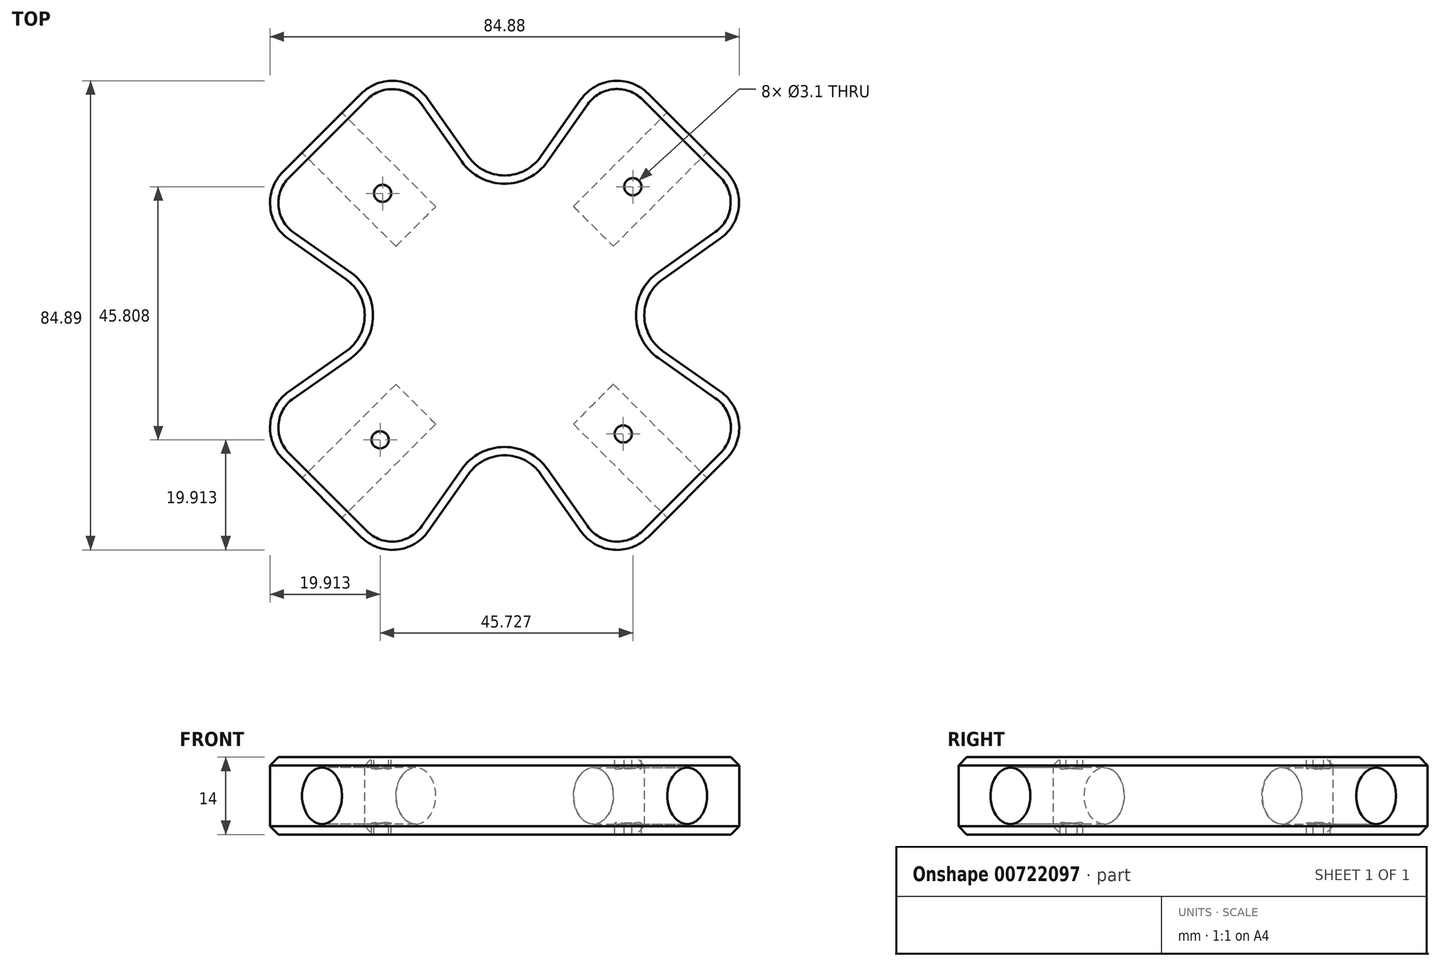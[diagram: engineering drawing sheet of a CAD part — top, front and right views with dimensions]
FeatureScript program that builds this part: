
annotation { "Feature Type Name" : "Feature", "Feature Type Description" : "" }
export const myFeature = defineFeature(function(context is Context, id is Id, definition is map)
    precondition{}
    {
        {
            var Q0;
            Q0=qCreatedBy(makeId("Top.planeOp"),FACE);
            var sketch = newSketch(context, id + "F0", { "sketchPlane" : qUnion([Q0])});
            skLineSegment(sketch, "E0", {"start": v(0, 0) * mm, "end": v(38.75, 38.75) * mm});
            skLineSegment(sketch, "E1", {"start": v(0, 0) * mm, "end": v(38.75, -38.75) * mm});
            skLineSegment(sketch, "E2", {"start": v(0, 0) * mm, "end": v(-38.75, -38.75) * mm});
            skLineSegment(sketch, "E3", {"start": v(0, 0) * mm, "end": v(-38.75, 38.75) * mm});
            skCircle(sketch, "E4.cCircle", {"center": v(0, 0) * mm, "radius": 54.8 * mm, "construction": true});
            skLineSegment(sketch, "E4.0", {"start": v(0, 54.8) * mm, "end": v(38.75, 38.75) * mm});
            skLineSegment(sketch, "E4.1", {"start": v(38.75, 38.75) * mm, "end": v(46.78, 19.38) * mm});
            skLineSegment(sketch, "E4.2", {"start": v(54.8, 0) * mm, "end": v(46.84, -19.24) * mm});
            skLineSegment(sketch, "E4.3", {"start": v(38.75, -38.75) * mm, "end": v(19.24, -46.84) * mm});
            skLineSegment(sketch, "E4.4", {"start": v(0, -54.8) * mm, "end": v(-19.24, -46.84) * mm});
            skLineSegment(sketch, "E4.5", {"start": v(-38.75, -38.75) * mm, "end": v(-46.84, -19.24) * mm});
            skLineSegment(sketch, "E4.6", {"start": v(-54.8, 0) * mm, "end": v(-38.75, 38.75) * mm});
            skLineSegment(sketch, "E4.7", {"start": v(-38.75, 38.75) * mm, "end": v(0, 54.8) * mm});
            skCircle(sketch, "E5.cCircle", {"center": v(-54.8, 0) * mm, "radius": 22.22 * mm, "construction": true});
            skLineSegment(sketch, "E5.0", {"start": v(-32.58, 0) * mm, "end": v(-43.7, -19.24) * mm});
            skLineSegment(sketch, "E5.1", {"start": v(-43.7, -19.24) * mm, "end": v(-65.92, -19.24) * mm});
            skLineSegment(sketch, "E5.2", {"start": v(-65.92, -19.24) * mm, "end": v(-77.03, 0) * mm});
            skLineSegment(sketch, "E5.3", {"start": v(-77.03, 0) * mm, "end": v(-65.92, 19.24) * mm});
            skLineSegment(sketch, "E5.4", {"start": v(-65.92, 19.24) * mm, "end": v(-46.84, 19.24) * mm});
            skLineSegment(sketch, "E5.5", {"start": v(-43.7, 19.24) * mm, "end": v(-32.58, 0) * mm});
            skCircle(sketch, "E6.cCircle", {"center": v(0, -54.8) * mm, "radius": 22.22 * mm, "construction": true});
            skLineSegment(sketch, "E6.0", {"start": v(0, -32.58) * mm, "end": v(19.24, -43.7) * mm});
            skLineSegment(sketch, "E6.1", {"start": v(19.24, -43.7) * mm, "end": v(19.24, -65.92) * mm});
            skLineSegment(sketch, "E6.2", {"start": v(19.24, -65.92) * mm, "end": v(0, -77.03) * mm});
            skLineSegment(sketch, "E6.3", {"start": v(0, -77.03) * mm, "end": v(-19.24, -65.92) * mm});
            skLineSegment(sketch, "E6.4", {"start": v(-19.24, -65.92) * mm, "end": v(-19.24, -43.7) * mm});
            skLineSegment(sketch, "E6.5", {"start": v(-19.24, -43.7) * mm, "end": v(0, -32.58) * mm});
            skCircle(sketch, "E7.cCircle", {"center": v(54.8, 0) * mm, "radius": 22.22 * mm, "construction": true});
            skLineSegment(sketch, "E7.0", {"start": v(32.58, 0) * mm, "end": v(43.7, 19.24) * mm});
            skLineSegment(sketch, "E7.1", {"start": v(43.7, 19.24) * mm, "end": v(65.92, 19.24) * mm});
            skLineSegment(sketch, "E7.2", {"start": v(65.92, 19.24) * mm, "end": v(77.03, 0) * mm});
            skLineSegment(sketch, "E7.3", {"start": v(77.03, 0) * mm, "end": v(65.92, -19.24) * mm});
            skLineSegment(sketch, "E7.4", {"start": v(65.92, -19.24) * mm, "end": v(43.7, -19.24) * mm});
            skLineSegment(sketch, "E7.5", {"start": v(43.7, -19.24) * mm, "end": v(32.58, 0) * mm});
            skCircle(sketch, "E8.cCircle", {"center": v(0, 54.8) * mm, "radius": 22.22 * mm, "construction": true});
            skLineSegment(sketch, "E8.0", {"start": v(0, 32.58) * mm, "end": v(-19.24, 43.7) * mm});
            skLineSegment(sketch, "E8.1", {"start": v(-19.24, 43.7) * mm, "end": v(-19.24, 46.84) * mm});
            skLineSegment(sketch, "E8.2", {"start": v(-19.24, 65.92) * mm, "end": v(0, 77.03) * mm});
            skLineSegment(sketch, "E8.3", {"start": v(0, 77.03) * mm, "end": v(19.24, 65.92) * mm});
            skLineSegment(sketch, "E8.4", {"start": v(19.24, 65.92) * mm, "end": v(19.24, 46.84) * mm});
            skLineSegment(sketch, "E8.5", {"start": v(19.24, 43.7) * mm, "end": v(0, 32.58) * mm});
            skLineSegment(sketch, "E9", {"start": v(-46.84, 19.24) * mm, "end": v(-43.7, 19.24) * mm});
            skLineSegment(sketch, "E10", {"start": v(-46.84, -19.24) * mm, "end": v(-54.8, 0) * mm});
            skLineSegment(sketch, "E11", {"start": v(-19.24, 46.84) * mm, "end": v(-19.24, 65.92) * mm});
            skLineSegment(sketch, "E12", {"start": v(19.24, 46.84) * mm, "end": v(19.24, 43.7) * mm});
            skLineSegment(sketch, "E13", {"start": v(46.78, 19.38) * mm, "end": v(54.8, 0) * mm});
            skLineSegment(sketch, "E14", {"start": v(46.84, -19.24) * mm, "end": v(38.75, -38.75) * mm});
            skLineSegment(sketch, "E15", {"start": v(19.24, -46.84) * mm, "end": v(0, -54.8) * mm});
            skLineSegment(sketch, "E16", {"start": v(-19.24, -46.84) * mm, "end": v(-38.75, -38.75) * mm});
            skLineSegment(sketch, "E17", {"start": v(-46.84, 19.24) * mm, "end": v(-19.24, 46.84) * mm});
            skLineSegment(sketch, "E18", {"start": v(19.24, 46.84) * mm, "end": v(46.78, 19.38) * mm});
            skLineSegment(sketch, "E19", {"start": v(46.84, -19.24) * mm, "end": v(19.24, -46.84) * mm});
            skLineSegment(sketch, "E20", {"start": v(-46.84, -19.24) * mm, "end": v(-19.24, -46.84) * mm});
            skLineSegment(sketch, "E21.bottom", {"start": v(19.38, -19.38) * mm, "end": v(-19.38, -19.38) * mm});
            skLineSegment(sketch, "E21.top", {"start": v(19.38, 19.38) * mm, "end": v(-19.38, 19.38) * mm});
            skLineSegment(sketch, "E21.left", {"start": v(19.38, -19.38) * mm, "end": v(19.38, 19.38) * mm});
            skLineSegment(sketch, "E21.right", {"start": v(-19.38, -19.38) * mm, "end": v(-19.38, 19.38) * mm});
            skLineSegment(sketch, "E22", {"start": v(-46.84, 19.24) * mm, "end": v(-19.38, 0) * mm});
            skLineSegment(sketch, "E23", {"start": v(-19.38, 0) * mm, "end": v(-46.84, -19.24) * mm});
            skLineSegment(sketch, "E24", {"start": v(-19.24, -46.84) * mm, "end": v(0, -19.38) * mm});
            skLineSegment(sketch, "E25", {"start": v(19.24, -46.84) * mm, "end": v(0, -19.38) * mm});
            skLineSegment(sketch, "E26", {"start": v(46.84, -19.24) * mm, "end": v(19.38, 0) * mm});
            skLineSegment(sketch, "E27", {"start": v(46.78, 19.38) * mm, "end": v(19.38, 0) * mm});
            skLineSegment(sketch, "E28", {"start": v(19.24, 46.84) * mm, "end": v(0, 19.38) * mm});
            skLineSegment(sketch, "E29", {"start": v(0, 19.38) * mm, "end": v(-19.24, 46.84) * mm});
            skSolve(sketch);
        }
        {
            var Q0;
            {var subQ0=sQuery(id+"F0.wireOp",EDGE,"E9");Q0=makeQuery(id+"F0.imprint","IMPRINT",FACE,{"disambiguationData":[TD([[makeQuery(id+"F0.imprint","IMPRINT",EDGE,{"derivedFrom":subQ0}),1.0]])]});}
            var Q1;
            {var subQ1=sQuery(id+"F0.wireOp",EDGE,"E2");var subQ3=sQuery(id+"F0.wireOp",EDGE,"E21.right");var subQ4=makeQuery(id+"F0.imprint","INTERSECT",VERTEX,{"derivedFrom":[subQ1,sQuery(id+"F0.wireOp",EDGE,"E21.bottom"),subQ3]});Q1=makeQuery(id+"F0.imprint","IMPRINT",FACE,{"disambiguationData":[TD([[makeQuery(id+"F0.imprint","IMPRINT",EDGE,{"disambiguationData":[TD([[subQ4,-1.0]])],"derivedFrom":subQ3}),-1.0]])]});}
            var Q2;
            {var subQ2=sQuery(id+"F0.wireOp",EDGE,"E5.1");var subQ6=sQuery(id+"F0.wireOp",EDGE,"E5.0");var subQ7=makeQuery(id+"F0.imprint","INTERSECT",VERTEX,{"derivedFrom":[subQ6,subQ2]});Q2=makeQuery(id+"F0.imprint","IMPRINT",FACE,{"disambiguationData":[TD([[makeQuery(id+"F0.imprint","IMPRINT",EDGE,{"disambiguationData":[TD([[subQ7,1.0]])],"derivedFrom":subQ6}),1.0]])]});}
            var Q3;
            {var subQ0=sQuery(id+"F0.wireOp",EDGE,"E6.5");var subQ1=sQuery(id+"F0.wireOp",EDGE,"E6.4");var subQ2=makeQuery(id+"F0.imprint","INTERSECT",VERTEX,{"derivedFrom":[subQ1,subQ0]});Q3=makeQuery(id+"F0.imprint","IMPRINT",FACE,{"disambiguationData":[TD([[makeQuery(id+"F0.imprint","IMPRINT",EDGE,{"disambiguationData":[TD([[subQ2,-1.0]])],"derivedFrom":subQ0}),1.0]])]});}
            var Q4;
            {var subQ2=sQuery(id+"F0.wireOp",EDGE,"E6.1");var subQ6=sQuery(id+"F0.wireOp",EDGE,"E6.0");var subQ7=makeQuery(id+"F0.imprint","INTERSECT",VERTEX,{"derivedFrom":[subQ6,subQ2]});Q4=makeQuery(id+"F0.imprint","IMPRINT",FACE,{"disambiguationData":[TD([[makeQuery(id+"F0.imprint","IMPRINT",EDGE,{"disambiguationData":[TD([[subQ7,1.0]])],"derivedFrom":subQ6}),1.0]])]});}
            var Q5;
            {var subQ0=sQuery(id+"F0.wireOp",EDGE,"E1");var subQ3=sQuery(id+"F0.wireOp",EDGE,"E21.left");var subQ5=makeQuery(id+"F0.imprint","INTERSECT",VERTEX,{"derivedFrom":[subQ0,sQuery(id+"F0.wireOp",EDGE,"E21.bottom"),subQ3]});Q5=makeQuery(id+"F0.imprint","IMPRINT",FACE,{"disambiguationData":[TD([[makeQuery(id+"F0.imprint","IMPRINT",EDGE,{"disambiguationData":[TD([[subQ5,-1.0]])],"derivedFrom":subQ3}),1.0]])]});}
            var Q6;
            {var subQ1=sQuery(id+"F0.wireOp",EDGE,"E1");var subQ3=sQuery(id+"F0.wireOp",EDGE,"E21.bottom");var subQ4=makeQuery(id+"F0.imprint","INTERSECT",VERTEX,{"derivedFrom":[subQ1,subQ3,sQuery(id+"F0.wireOp",EDGE,"E21.left")]});Q6=makeQuery(id+"F0.imprint","IMPRINT",FACE,{"disambiguationData":[TD([[makeQuery(id+"F0.imprint","IMPRINT",EDGE,{"disambiguationData":[TD([[subQ4,-1.0]])],"derivedFrom":subQ3}),-1.0]])]});}
            var Q7;
            {var subQ1=sQuery(id+"F0.wireOp",EDGE,"E0");var subQ3=sQuery(id+"F0.wireOp",EDGE,"E21.top");var subQ4=makeQuery(id+"F0.imprint","INTERSECT",VERTEX,{"derivedFrom":[subQ1,subQ3,sQuery(id+"F0.wireOp",EDGE,"E21.left")]});Q7=makeQuery(id+"F0.imprint","IMPRINT",FACE,{"disambiguationData":[TD([[makeQuery(id+"F0.imprint","IMPRINT",EDGE,{"disambiguationData":[TD([[subQ4,-1.0]])],"derivedFrom":subQ3}),1.0]])]});}
            var Q8;
            {var subQ0=sQuery(id+"F0.wireOp",EDGE,"E7.1");var subQ1=sQuery(id+"F0.wireOp",EDGE,"E7.0");var subQ2=makeQuery(id+"F0.imprint","INTERSECT",VERTEX,{"derivedFrom":[subQ1,subQ0]});Q8=makeQuery(id+"F0.imprint","IMPRINT",FACE,{"disambiguationData":[TD([[makeQuery(id+"F0.imprint","IMPRINT",EDGE,{"disambiguationData":[TD([[subQ2,1.0]])],"derivedFrom":subQ1}),1.0]])]});}
            var Q9;
            {var subQ2=sQuery(id+"F0.wireOp",EDGE,"E12");Q9=makeQuery(id+"F0.imprint","IMPRINT",FACE,{"disambiguationData":[TD([[makeQuery(id+"F0.imprint","IMPRINT",EDGE,{"derivedFrom":subQ2}),1.0]])]});}
            var Q10;
            {var subQ2=sQuery(id+"F0.wireOp",EDGE,"E8.1");Q10=makeQuery(id+"F0.imprint","IMPRINT",FACE,{"disambiguationData":[TD([[makeQuery(id+"F0.imprint","IMPRINT",EDGE,{"derivedFrom":subQ2}),1.0]])]});}
            var Q11;
            {var subQ0=sQuery(id+"F0.wireOp",EDGE,"E7.5");var subQ1=sQuery(id+"F0.wireOp",EDGE,"E7.4");var subQ2=makeQuery(id+"F0.imprint","INTERSECT",VERTEX,{"derivedFrom":[subQ1,subQ0]});Q11=makeQuery(id+"F0.imprint","IMPRINT",FACE,{"disambiguationData":[TD([[makeQuery(id+"F0.imprint","IMPRINT",EDGE,{"disambiguationData":[TD([[subQ2,-1.0]])],"derivedFrom":subQ0}),1.0]])]});}
            var Q12;
            {var subQ0=sQuery(id+"F0.wireOp",EDGE,"E9");Q12=makeQuery(id+"F0.imprint","IMPRINT",FACE,{"disambiguationData":[TD([[makeQuery(id+"F0.imprint","IMPRINT",EDGE,{"derivedFrom":subQ0}),-1.0]])]});}
            var Q13;
            {var subQ0=sQuery(id+"F0.wireOp",EDGE,"E8.1");Q13=makeQuery(id+"F0.imprint","IMPRINT",FACE,{"disambiguationData":[TD([[makeQuery(id+"F0.imprint","IMPRINT",EDGE,{"derivedFrom":subQ0}),-1.0]])]});}
            var Q14;
            {var subQ0=sQuery(id+"F0.wireOp",EDGE,"E12");Q14=makeQuery(id+"F0.imprint","IMPRINT",FACE,{"disambiguationData":[TD([[makeQuery(id+"F0.imprint","IMPRINT",EDGE,{"derivedFrom":subQ0}),-1.0]])]});}
            var Q15;
            {var subQ0=sQuery(id+"F0.wireOp",EDGE,"E7.1");var subQ1=sQuery(id+"F0.wireOp",EDGE,"E7.0");var subQ2=makeQuery(id+"F0.imprint","INTERSECT",VERTEX,{"derivedFrom":[subQ1,subQ0]});Q15=makeQuery(id+"F0.imprint","IMPRINT",FACE,{"disambiguationData":[TD([[makeQuery(id+"F0.imprint","IMPRINT",EDGE,{"disambiguationData":[TD([[subQ2,1.0]])],"derivedFrom":subQ1}),-1.0]])]});}
            var Q16;
            {var subQ1=sQuery(id+"F0.wireOp",EDGE,"E7.4");var subQ3=sQuery(id+"F0.wireOp",EDGE,"E7.5");var subQ4=makeQuery(id+"F0.imprint","INTERSECT",VERTEX,{"derivedFrom":[subQ1,subQ3]});Q16=makeQuery(id+"F0.imprint","IMPRINT",FACE,{"disambiguationData":[TD([[makeQuery(id+"F0.imprint","IMPRINT",EDGE,{"disambiguationData":[TD([[subQ4,-1.0]])],"derivedFrom":subQ3}),-1.0]])]});}
            var Q17;
            {var subQ0=sQuery(id+"F0.wireOp",EDGE,"E6.1");var subQ1=sQuery(id+"F0.wireOp",EDGE,"E6.0");var subQ2=makeQuery(id+"F0.imprint","INTERSECT",VERTEX,{"derivedFrom":[subQ1,subQ0]});Q17=makeQuery(id+"F0.imprint","IMPRINT",FACE,{"disambiguationData":[TD([[makeQuery(id+"F0.imprint","IMPRINT",EDGE,{"disambiguationData":[TD([[subQ2,1.0]])],"derivedFrom":subQ1}),-1.0]])]});}
            var Q18;
            {var subQ1=sQuery(id+"F0.wireOp",EDGE,"E6.4");var subQ3=sQuery(id+"F0.wireOp",EDGE,"E6.5");var subQ4=makeQuery(id+"F0.imprint","INTERSECT",VERTEX,{"derivedFrom":[subQ1,subQ3]});Q18=makeQuery(id+"F0.imprint","IMPRINT",FACE,{"disambiguationData":[TD([[makeQuery(id+"F0.imprint","IMPRINT",EDGE,{"disambiguationData":[TD([[subQ4,-1.0]])],"derivedFrom":subQ3}),-1.0]])]});}
            var Q19;
            {var subQ0=sQuery(id+"F0.wireOp",EDGE,"E5.1");var subQ1=sQuery(id+"F0.wireOp",EDGE,"E5.0");var subQ2=makeQuery(id+"F0.imprint","INTERSECT",VERTEX,{"derivedFrom":[subQ1,subQ0]});Q19=makeQuery(id+"F0.imprint","IMPRINT",FACE,{"disambiguationData":[TD([[makeQuery(id+"F0.imprint","IMPRINT",EDGE,{"disambiguationData":[TD([[subQ2,1.0]])],"derivedFrom":subQ1}),-1.0]])]});}
            extrude(context, id + "F1", {"entities" : qUnion([Q0, Q1, Q2, Q3, Q4, Q5, Q6, Q7, Q8, Q9, Q10, Q11, Q12, Q13, Q14, Q15, Q16, Q17, Q18, Q19]), "depth" : 14 * mm, "offsetDistance" : 25 * mm});
        }
        {
            var Q0;
            Q0=makeQuery(id+"F1.opExtrude","SWEPT_FACE",FACE,{"disambiguationData":[OSD([sQuery(id+"F0.wireOp",EDGE,"E20")])]});
            var sketch = newSketch(context, id + "F2", { "sketchPlane" : qUnion([Q0])});
            skLineSegment(sketch, "E30", {"start": v(0, 7) * mm, "end": v(19.5, 7) * mm});
            skPoint(sketch, "E30.startSnap0", {"position": v(-19.5, 7) * mm});
            skCircle(sketch, "E31", {"center": v(0, 7) * mm, "radius": 5.1 * mm});
            skSolve(sketch);
        }
        {
            var Q0;
            Q0=makeQuery(id+"F1.opExtrude","SWEPT_FACE",FACE,{"disambiguationData":[OSD([sQuery(id+"F0.wireOp",EDGE,"E19")])]});
            var sketch = newSketch(context, id + "F3", { "sketchPlane" : qUnion([Q0])});
            skCircle(sketch, "E32", {"center": v(0, 7) * mm, "radius": 5.1 * mm});
            skPoint(sketch, "E32.centerSnap0", {"position": v(-19.5, 7) * mm});
            skPoint(sketch, "E32.centerSnap1", {"position": v(0, 14) * mm});
            skSolve(sketch);
        }
        {
            var Q0;
            Q0=makeQuery(id+"F1.opExtrude","SWEPT_FACE",FACE,{"disambiguationData":[OSD([sQuery(id+"F0.wireOp",EDGE,"E18")])]});
            var sketch = newSketch(context, id + "F4", { "sketchPlane" : qUnion([Q0])});
            skCircle(sketch, "E33", {"center": v(0, 7) * mm, "radius": 5.1 * mm});
            skPoint(sketch, "E33.centerSnap0", {"position": v(-19.44, 7) * mm});
            skPoint(sketch, "E33.centerSnap1", {"position": v(0, 14) * mm});
            skSolve(sketch);
        }
        {
            var Q0;
            Q0=makeQuery(id+"F1.opExtrude","SWEPT_FACE",FACE,{"disambiguationData":[OSD([sQuery(id+"F0.wireOp",EDGE,"E17")])]});
            var sketch = newSketch(context, id + "F5", { "sketchPlane" : qUnion([Q0])});
            skCircle(sketch, "E34", {"center": v(0, 7) * mm, "radius": 5.1 * mm});
            skPoint(sketch, "E34.centerSnap0", {"position": v(-19.5, 7) * mm});
            skPoint(sketch, "E34.centerSnap1", {"position": v(0, 14) * mm});
            skSolve(sketch);
        }
        {
            var Q0;
            Q0=makeQuery(id+"F2.imprint","IMPRINT",FACE,{"disambiguationData":[TD([[makeQuery(id+"F2.imprint","IMPRINT",EDGE,{"derivedFrom":sQuery(id+"F2.wireOp",EDGE,"E31")}),1.0]])]});
            extrude(context, id + "F6", {"entities" : qUnion([Q0]), "operationType" : NewBodyOperationType.REMOVE, "oppositeDirection" : true, "depth" : 24 * mm, "offsetDistance" : 25 * mm});
        }
        {
            var Q0;
            Q0=makeQuery(id+"F1.opExtrude","SWEPT_EDGE",EDGE,{"disambiguationData":[OSD([sQuery(id+"F0.wireOp",EDGE,"E4.5"),sQuery(id+"F0.wireOp",EDGE,"E5.1"),sQuery(id+"F0.wireOp",EDGE,"E10"),sQuery(id+"F0.wireOp",EDGE,"E20"),sQuery(id+"F0.wireOp",EDGE,"E23")])]});
            var Q1;
            Q1=makeQuery(id+"F1.opExtrude","SWEPT_EDGE",EDGE,{"disambiguationData":[OSD([sQuery(id+"F0.wireOp",EDGE,"E21.right"),sQuery(id+"F0.wireOp",EDGE,"E22"),sQuery(id+"F0.wireOp",EDGE,"E23")])]});
            var Q2;
            Q2=makeQuery(id+"F1.opExtrude","SWEPT_EDGE",EDGE,{"disambiguationData":[OSD([sQuery(id+"F0.wireOp",EDGE,"E4.6"),sQuery(id+"F0.wireOp",EDGE,"E5.4"),sQuery(id+"F0.wireOp",EDGE,"E9"),sQuery(id+"F0.wireOp",EDGE,"E17"),sQuery(id+"F0.wireOp",EDGE,"E22")])]});
            var Q3;
            Q3=makeQuery(id+"F1.opExtrude","SWEPT_EDGE",EDGE,{"disambiguationData":[OSD([sQuery(id+"F0.wireOp",EDGE,"E4.7"),sQuery(id+"F0.wireOp",EDGE,"E8.1"),sQuery(id+"F0.wireOp",EDGE,"E11"),sQuery(id+"F0.wireOp",EDGE,"E17"),sQuery(id+"F0.wireOp",EDGE,"E29")])]});
            var Q4;
            Q4=makeQuery(id+"F1.opExtrude","SWEPT_EDGE",EDGE,{"disambiguationData":[OSD([sQuery(id+"F0.wireOp",EDGE,"E21.top"),sQuery(id+"F0.wireOp",EDGE,"E28"),sQuery(id+"F0.wireOp",EDGE,"E29")])]});
            var Q5;
            Q5=makeQuery(id+"F1.opExtrude","SWEPT_EDGE",EDGE,{"disambiguationData":[OSD([sQuery(id+"F0.wireOp",EDGE,"E4.0"),sQuery(id+"F0.wireOp",EDGE,"E8.4"),sQuery(id+"F0.wireOp",EDGE,"E12"),sQuery(id+"F0.wireOp",EDGE,"E18"),sQuery(id+"F0.wireOp",EDGE,"E28")])]});
            var Q6;
            Q6=makeQuery(id+"F1.opExtrude","SWEPT_EDGE",EDGE,{"disambiguationData":[OSD([sQuery(id+"F0.wireOp",EDGE,"E4.1"),sQuery(id+"F0.wireOp",EDGE,"E13"),sQuery(id+"F0.wireOp",EDGE,"E18"),sQuery(id+"F0.wireOp",EDGE,"E27")])]});
            var Q7;
            Q7=makeQuery(id+"F1.opExtrude","SWEPT_EDGE",EDGE,{"disambiguationData":[OSD([sQuery(id+"F0.wireOp",EDGE,"E21.left"),sQuery(id+"F0.wireOp",EDGE,"E26"),sQuery(id+"F0.wireOp",EDGE,"E27")])]});
            var Q8;
            Q8=makeQuery(id+"F1.opExtrude","SWEPT_EDGE",EDGE,{"disambiguationData":[OSD([sQuery(id+"F0.wireOp",EDGE,"E4.2"),sQuery(id+"F0.wireOp",EDGE,"E7.4"),sQuery(id+"F0.wireOp",EDGE,"E14"),sQuery(id+"F0.wireOp",EDGE,"E19"),sQuery(id+"F0.wireOp",EDGE,"E26")])]});
            var Q9;
            Q9=makeQuery(id+"F1.opExtrude","SWEPT_EDGE",EDGE,{"disambiguationData":[OSD([sQuery(id+"F0.wireOp",EDGE,"E4.3"),sQuery(id+"F0.wireOp",EDGE,"E6.1"),sQuery(id+"F0.wireOp",EDGE,"E15"),sQuery(id+"F0.wireOp",EDGE,"E19"),sQuery(id+"F0.wireOp",EDGE,"E25")])]});
            var Q10;
            Q10=makeQuery(id+"F1.opExtrude","SWEPT_EDGE",EDGE,{"disambiguationData":[OSD([sQuery(id+"F0.wireOp",EDGE,"E21.bottom"),sQuery(id+"F0.wireOp",EDGE,"E24"),sQuery(id+"F0.wireOp",EDGE,"E25")])]});
            var Q11;
            Q11=makeQuery(id+"F1.opExtrude","SWEPT_EDGE",EDGE,{"disambiguationData":[OSD([sQuery(id+"F0.wireOp",EDGE,"E4.4"),sQuery(id+"F0.wireOp",EDGE,"E6.4"),sQuery(id+"F0.wireOp",EDGE,"E16"),sQuery(id+"F0.wireOp",EDGE,"E20"),sQuery(id+"F0.wireOp",EDGE,"E24")])]});
            fillet(context, id + "F7", {"entities" : qUnion([Q0, Q1, Q2, Q3, Q4, Q5, Q6, Q7, Q8, Q9, Q10, Q11]), "radius" : 8 * mm, "tangentPropagation" : true, "allowEdgeOverflow" : false});
        }
        {
            var Q0;
            {var subQ0=sQuery(id+"F0.wireOp",EDGE,"E24");var subQ1=sQuery(id+"F0.wireOp",EDGE,"E20");Q0=makeQuery(id+"F7.opFillet","BLEND_EDGE",EDGE,{"blendedFrom":[makeQuery(id+"F1.opExtrude","SWEPT_EDGE",EDGE,{"disambiguationData":[OSD([sQuery(id+"F0.wireOp",EDGE,"E4.4"),sQuery(id+"F0.wireOp",EDGE,"E6.4"),sQuery(id+"F0.wireOp",EDGE,"E16"),subQ1,subQ0])]}),makeQuery(id+"F1.opExtrude","CAP_FACE",FACE,{"disambiguationData":[OSD([sQuery(id+"F0.wireOp",EDGE,"E17"),sQuery(id+"F0.wireOp",EDGE,"E18"),sQuery(id+"F0.wireOp",EDGE,"E19"),subQ1,sQuery(id+"F0.wireOp",EDGE,"E22"),sQuery(id+"F0.wireOp",EDGE,"E23"),subQ0,sQuery(id+"F0.wireOp",EDGE,"E25"),sQuery(id+"F0.wireOp",EDGE,"E26"),sQuery(id+"F0.wireOp",EDGE,"E27"),sQuery(id+"F0.wireOp",EDGE,"E28"),sQuery(id+"F0.wireOp",EDGE,"E29")])],"isStart":false})],"blendedInto":[makeQuery(id+"F1.opExtrude","CAP_FACE",FACE,{"disambiguationData":[OSD([sQuery(id+"F0.wireOp",EDGE,"E17"),sQuery(id+"F0.wireOp",EDGE,"E18"),sQuery(id+"F0.wireOp",EDGE,"E19"),subQ1,sQuery(id+"F0.wireOp",EDGE,"E22"),sQuery(id+"F0.wireOp",EDGE,"E23"),subQ0,sQuery(id+"F0.wireOp",EDGE,"E25"),sQuery(id+"F0.wireOp",EDGE,"E26"),sQuery(id+"F0.wireOp",EDGE,"E27"),sQuery(id+"F0.wireOp",EDGE,"E28"),sQuery(id+"F0.wireOp",EDGE,"E29")])],"isStart":false})]});}
            var Q1;
            Q1=makeQuery(id+"F1.opExtrude","CAP_EDGE",EDGE,{"disambiguationData":[OSD([sQuery(id+"F0.wireOp",EDGE,"E22")])],"isStart":false});
            var Q2;
            Q2=makeQuery(id+"F1.opExtrude","CAP_EDGE",EDGE,{"disambiguationData":[OSD([sQuery(id+"F0.wireOp",EDGE,"E28")])],"isStart":false});
            var Q3;
            Q3=makeQuery(id+"F1.opExtrude","CAP_EDGE",EDGE,{"disambiguationData":[OSD([sQuery(id+"F0.wireOp",EDGE,"E19")])],"isStart":false});
            var Q4;
            {var subQ0=sQuery(id+"F0.wireOp",EDGE,"E25");var subQ1=sQuery(id+"F0.wireOp",EDGE,"E19");Q4=makeQuery(id+"F7.opFillet","BLEND_EDGE",EDGE,{"blendedFrom":[makeQuery(id+"F1.opExtrude","SWEPT_EDGE",EDGE,{"disambiguationData":[OSD([sQuery(id+"F0.wireOp",EDGE,"E4.3"),sQuery(id+"F0.wireOp",EDGE,"E6.1"),sQuery(id+"F0.wireOp",EDGE,"E15"),subQ1,subQ0])]}),makeQuery(id+"F1.opExtrude","CAP_FACE",FACE,{"disambiguationData":[OSD([sQuery(id+"F0.wireOp",EDGE,"E17"),sQuery(id+"F0.wireOp",EDGE,"E18"),subQ1,sQuery(id+"F0.wireOp",EDGE,"E20"),sQuery(id+"F0.wireOp",EDGE,"E22"),sQuery(id+"F0.wireOp",EDGE,"E23"),sQuery(id+"F0.wireOp",EDGE,"E24"),subQ0,sQuery(id+"F0.wireOp",EDGE,"E26"),sQuery(id+"F0.wireOp",EDGE,"E27"),sQuery(id+"F0.wireOp",EDGE,"E28"),sQuery(id+"F0.wireOp",EDGE,"E29")])],"isStart":true})],"blendedInto":[makeQuery(id+"F1.opExtrude","CAP_FACE",FACE,{"disambiguationData":[OSD([sQuery(id+"F0.wireOp",EDGE,"E17"),sQuery(id+"F0.wireOp",EDGE,"E18"),subQ1,sQuery(id+"F0.wireOp",EDGE,"E20"),sQuery(id+"F0.wireOp",EDGE,"E22"),sQuery(id+"F0.wireOp",EDGE,"E23"),sQuery(id+"F0.wireOp",EDGE,"E24"),subQ0,sQuery(id+"F0.wireOp",EDGE,"E26"),sQuery(id+"F0.wireOp",EDGE,"E27"),sQuery(id+"F0.wireOp",EDGE,"E28"),sQuery(id+"F0.wireOp",EDGE,"E29")])],"isStart":true})]});}
            var Q5;
            {var subQ0=sQuery(id+"F0.wireOp",EDGE,"E27");var subQ1=sQuery(id+"F0.wireOp",EDGE,"E26");Q5=makeQuery(id+"F7.opFillet","BLEND_EDGE",EDGE,{"blendedFrom":[makeQuery(id+"F1.opExtrude","SWEPT_EDGE",EDGE,{"disambiguationData":[OSD([sQuery(id+"F0.wireOp",EDGE,"E21.left"),subQ1,subQ0])]}),makeQuery(id+"F1.opExtrude","CAP_FACE",FACE,{"disambiguationData":[OSD([sQuery(id+"F0.wireOp",EDGE,"E17"),sQuery(id+"F0.wireOp",EDGE,"E18"),sQuery(id+"F0.wireOp",EDGE,"E19"),sQuery(id+"F0.wireOp",EDGE,"E20"),sQuery(id+"F0.wireOp",EDGE,"E22"),sQuery(id+"F0.wireOp",EDGE,"E23"),sQuery(id+"F0.wireOp",EDGE,"E24"),sQuery(id+"F0.wireOp",EDGE,"E25"),subQ1,subQ0,sQuery(id+"F0.wireOp",EDGE,"E28"),sQuery(id+"F0.wireOp",EDGE,"E29")])],"isStart":true})],"blendedInto":[makeQuery(id+"F1.opExtrude","CAP_FACE",FACE,{"disambiguationData":[OSD([sQuery(id+"F0.wireOp",EDGE,"E17"),sQuery(id+"F0.wireOp",EDGE,"E18"),sQuery(id+"F0.wireOp",EDGE,"E19"),sQuery(id+"F0.wireOp",EDGE,"E20"),sQuery(id+"F0.wireOp",EDGE,"E22"),sQuery(id+"F0.wireOp",EDGE,"E23"),sQuery(id+"F0.wireOp",EDGE,"E24"),sQuery(id+"F0.wireOp",EDGE,"E25"),subQ1,subQ0,sQuery(id+"F0.wireOp",EDGE,"E28"),sQuery(id+"F0.wireOp",EDGE,"E29")])],"isStart":true})]});}
            var Q6;
            {var subQ0=sQuery(id+"F0.wireOp",EDGE,"E27");var subQ1=sQuery(id+"F0.wireOp",EDGE,"E18");Q6=makeQuery(id+"F7.opFillet","BLEND_EDGE",EDGE,{"blendedFrom":[makeQuery(id+"F1.opExtrude","SWEPT_EDGE",EDGE,{"disambiguationData":[OSD([sQuery(id+"F0.wireOp",EDGE,"E4.1"),sQuery(id+"F0.wireOp",EDGE,"E13"),subQ1,subQ0])]}),makeQuery(id+"F1.opExtrude","CAP_FACE",FACE,{"disambiguationData":[OSD([sQuery(id+"F0.wireOp",EDGE,"E17"),subQ1,sQuery(id+"F0.wireOp",EDGE,"E19"),sQuery(id+"F0.wireOp",EDGE,"E20"),sQuery(id+"F0.wireOp",EDGE,"E22"),sQuery(id+"F0.wireOp",EDGE,"E23"),sQuery(id+"F0.wireOp",EDGE,"E24"),sQuery(id+"F0.wireOp",EDGE,"E25"),sQuery(id+"F0.wireOp",EDGE,"E26"),subQ0,sQuery(id+"F0.wireOp",EDGE,"E28"),sQuery(id+"F0.wireOp",EDGE,"E29")])],"isStart":true})],"blendedInto":[makeQuery(id+"F1.opExtrude","CAP_FACE",FACE,{"disambiguationData":[OSD([sQuery(id+"F0.wireOp",EDGE,"E17"),subQ1,sQuery(id+"F0.wireOp",EDGE,"E19"),sQuery(id+"F0.wireOp",EDGE,"E20"),sQuery(id+"F0.wireOp",EDGE,"E22"),sQuery(id+"F0.wireOp",EDGE,"E23"),sQuery(id+"F0.wireOp",EDGE,"E24"),sQuery(id+"F0.wireOp",EDGE,"E25"),sQuery(id+"F0.wireOp",EDGE,"E26"),subQ0,sQuery(id+"F0.wireOp",EDGE,"E28"),sQuery(id+"F0.wireOp",EDGE,"E29")])],"isStart":true})]});}
            chamfer(context, id + "F8", {"entities" : qUnion([Q0, Q1, Q2, Q3, Q4, Q5, Q6]), "width" : 1.5 * mm, "tangentPropagation" : true});
        }
        {
            var Q0;
            Q0=makeQuery(id+"F4.imprint","IMPRINT",FACE,{"disambiguationData":[TD([[makeQuery(id+"F4.imprint","IMPRINT",EDGE,{"derivedFrom":sQuery(id+"F4.wireOp",EDGE,"E33")}),1.0]])]});
            var Q1;
            Q1=makeQuery(id+"F3.imprint","IMPRINT",FACE,{"disambiguationData":[TD([[makeQuery(id+"F3.imprint","IMPRINT",EDGE,{"derivedFrom":sQuery(id+"F3.wireOp",EDGE,"E32")}),1.0]])]});
            extrude(context, id + "F9", {"entities" : qUnion([Q0, Q1]), "operationType" : NewBodyOperationType.REMOVE, "oppositeDirection" : true, "depth" : 24 * mm, "offsetDistance" : 25 * mm});
        }
        {
            var Q0;
            Q0=makeQuery(id+"F3.imprint","IMPRINT",FACE,{"disambiguationData":[TD([[makeQuery(id+"F3.imprint","IMPRINT",EDGE,{"derivedFrom":sQuery(id+"F3.wireOp",EDGE,"E32")}),1.0]])]});
            extrude(context, id + "F10", {"entities" : qUnion([Q0]), "operationType" : NewBodyOperationType.REMOVE, "oppositeDirection" : true, "depth" : 24 * mm, "offsetDistance" : 25 * mm});
        }
        {
            var Q0;
            Q0=makeQuery(id+"F5.imprint","IMPRINT",FACE,{"disambiguationData":[TD([[makeQuery(id+"F5.imprint","IMPRINT",EDGE,{"derivedFrom":sQuery(id+"F5.wireOp",EDGE,"E34")}),1.0]])]});
            extrude(context, id + "F11", {"entities" : qUnion([Q0]), "operationType" : NewBodyOperationType.REMOVE, "oppositeDirection" : true, "depth" : 24 * mm, "offsetDistance" : 25 * mm});
        }
        {
            var Q0;
            Q0=makeQuery(id+"F1.opExtrude","CAP_FACE",FACE,{"disambiguationData":[OSD([sQuery(id+"F0.wireOp",EDGE,"E17"),sQuery(id+"F0.wireOp",EDGE,"E18"),sQuery(id+"F0.wireOp",EDGE,"E19"),sQuery(id+"F0.wireOp",EDGE,"E20"),sQuery(id+"F0.wireOp",EDGE,"E22"),sQuery(id+"F0.wireOp",EDGE,"E23"),sQuery(id+"F0.wireOp",EDGE,"E24"),sQuery(id+"F0.wireOp",EDGE,"E25"),sQuery(id+"F0.wireOp",EDGE,"E26"),sQuery(id+"F0.wireOp",EDGE,"E27"),sQuery(id+"F0.wireOp",EDGE,"E28"),sQuery(id+"F0.wireOp",EDGE,"E29")])],"isStart":false});
            var sketch = newSketch(context, id + "F12", { "sketchPlane" : qUnion([Q0])});
            skLineSegment(sketch, "E35", {"start": v(-31.98, 31.98) * mm, "end": v(-22.08, 22.08) * mm});
            skLineSegment(sketch, "E36", {"start": v(31.96, 32.04) * mm, "end": v(23.2, 23.28) * mm});
            skLineSegment(sketch, "E37", {"start": v(31.98, -31.98) * mm, "end": v(21.46, -21.46) * mm});
            skLineSegment(sketch, "E38", {"start": v(-31.98, -31.98) * mm, "end": v(-22.53, -22.53) * mm});
            skCircle(sketch, "E39", {"center": v(-22.08, 22.08) * mm, "radius": 1.55 * mm});
            skCircle(sketch, "E40", {"center": v(23.2, 23.28) * mm, "radius": 1.55 * mm});
            skCircle(sketch, "E41", {"center": v(21.46, -21.46) * mm, "radius": 1.55 * mm});
            skCircle(sketch, "E42", {"center": v(-22.53, -22.53) * mm, "radius": 1.55 * mm});
            skSolve(sketch);
        }
        {
            var Q0;
            Q0 = qSketchRegion(id + "F12", true);
            extrude(context, id + "F13", {"entities" : qUnion([Q0]), "operationType" : NewBodyOperationType.REMOVE, "oppositeDirection" : true, "depth" : 25 * mm, "offsetDistance" : 25 * mm});
        }
    });
